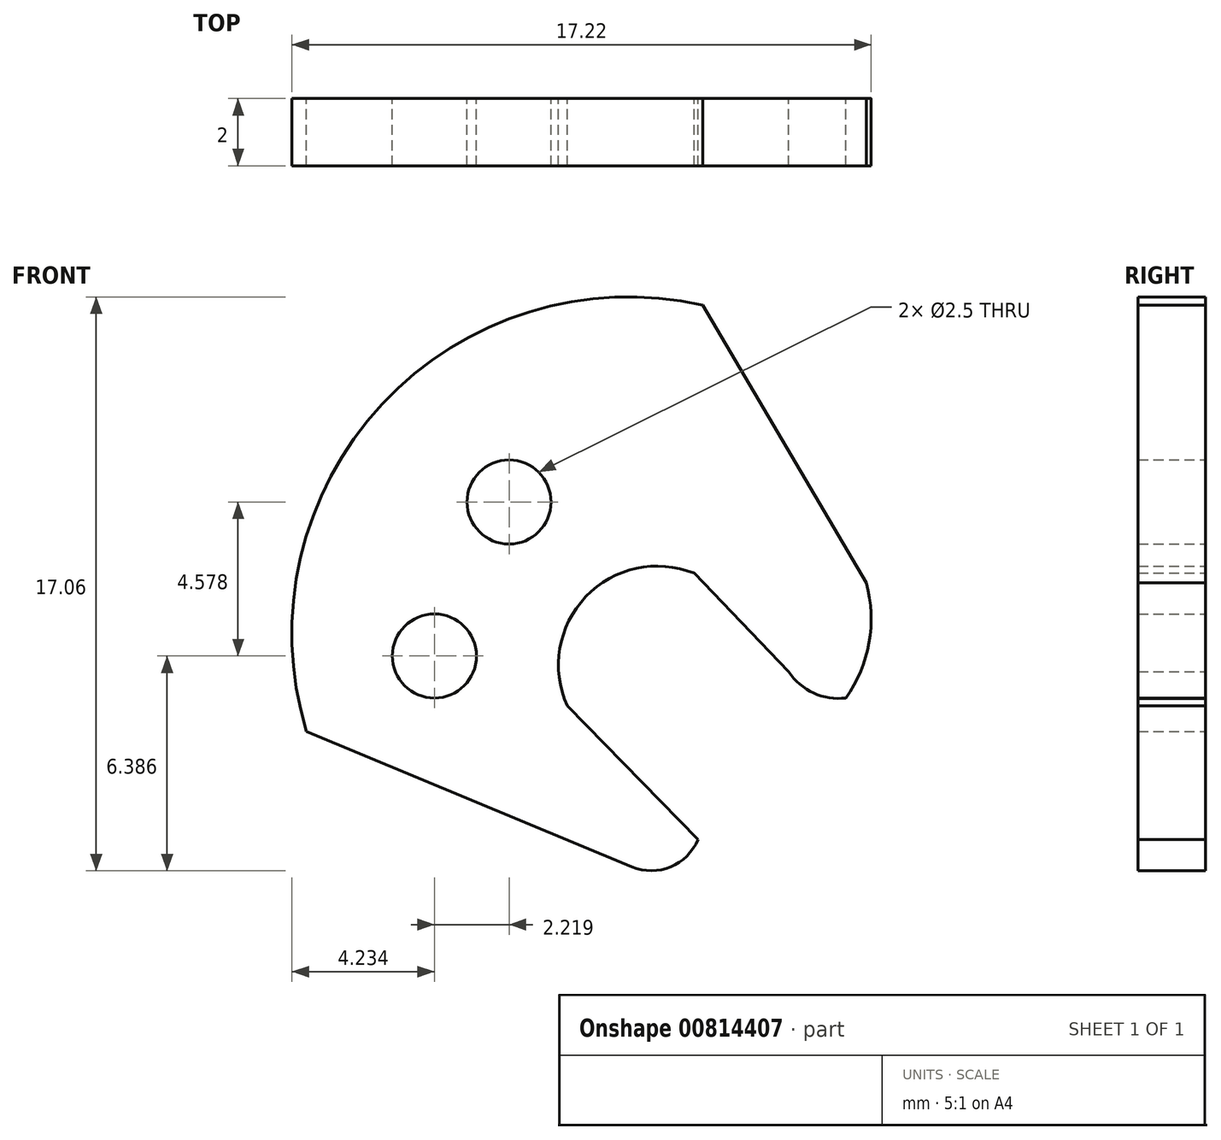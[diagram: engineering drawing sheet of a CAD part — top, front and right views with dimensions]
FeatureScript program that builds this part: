
annotation { "Feature Type Name" : "Feature", "Feature Type Description" : "" }
export const myFeature = defineFeature(function(context is Context, id is Id, definition is map)
    precondition{}
    {
        {
            var Q0;
            Q0=qCreatedBy(makeId("Front.planeOp"),FACE);
            var sketch = newSketch(context, id + "F0", { "sketchPlane" : qUnion([Q0])});
            skLineSegment(sketch, "E0", {"start": v(1.41, -8.44) * mm, "end": v(-8.26, -4.42) * mm});
            skArc(sketch, "E1", {"start": v(3.53, 8.26) * mm, "mid": v(-6.01, 5.31) * mm, "end": v(-8.26, -4.42) * mm});
            skLineSegment(sketch, "E2", {"start": v(3.53, 8.26) * mm, "end": v(8.39, 0) * mm});
            skArc(sketch, "E3", {"start": v(7.78, -3.42) * mm, "mid": v(8.47, -1.78) * mm, "end": v(8.39, 0) * mm});
            skArc(sketch, "E4", {"start": v(6.08, -2.64) * mm, "mid": v(6.82, -3.27) * mm, "end": v(7.78, -3.42) * mm});
            skLineSegment(sketch, "E5", {"start": v(6.08, -2.64) * mm, "end": v(3.27, 0.29) * mm});
            skArc(sketch, "E6", {"start": v(3.27, 0.29) * mm, "mid": v(0.05, -0.41) * mm, "end": v(-0.5, -3.66) * mm});
            skLineSegment(sketch, "E7", {"start": v(-0.5, -3.66) * mm, "end": v(3.38, -7.63) * mm});
            skArc(sketch, "E8", {"start": v(1.41, -8.44) * mm, "mid": v(2.56, -8.44) * mm, "end": v(3.38, -7.63) * mm});
            skCircle(sketch, "E9", {"center": v(-2.24, 2.4) * mm, "radius": 1.25 * mm});
            skCircle(sketch, "E10", {"center": v(-4.46, -2.17) * mm, "radius": 1.25 * mm});
            skSolve(sketch);
        }
        {
            var Q0;
            Q0 = qSketchRegion(id + "F0", true);
            extrude(context, id + "F1", {"entities" : qUnion([Q0]), "depth" : 2 * mm, "offsetDistance" : 25 * mm});
        }
    });
